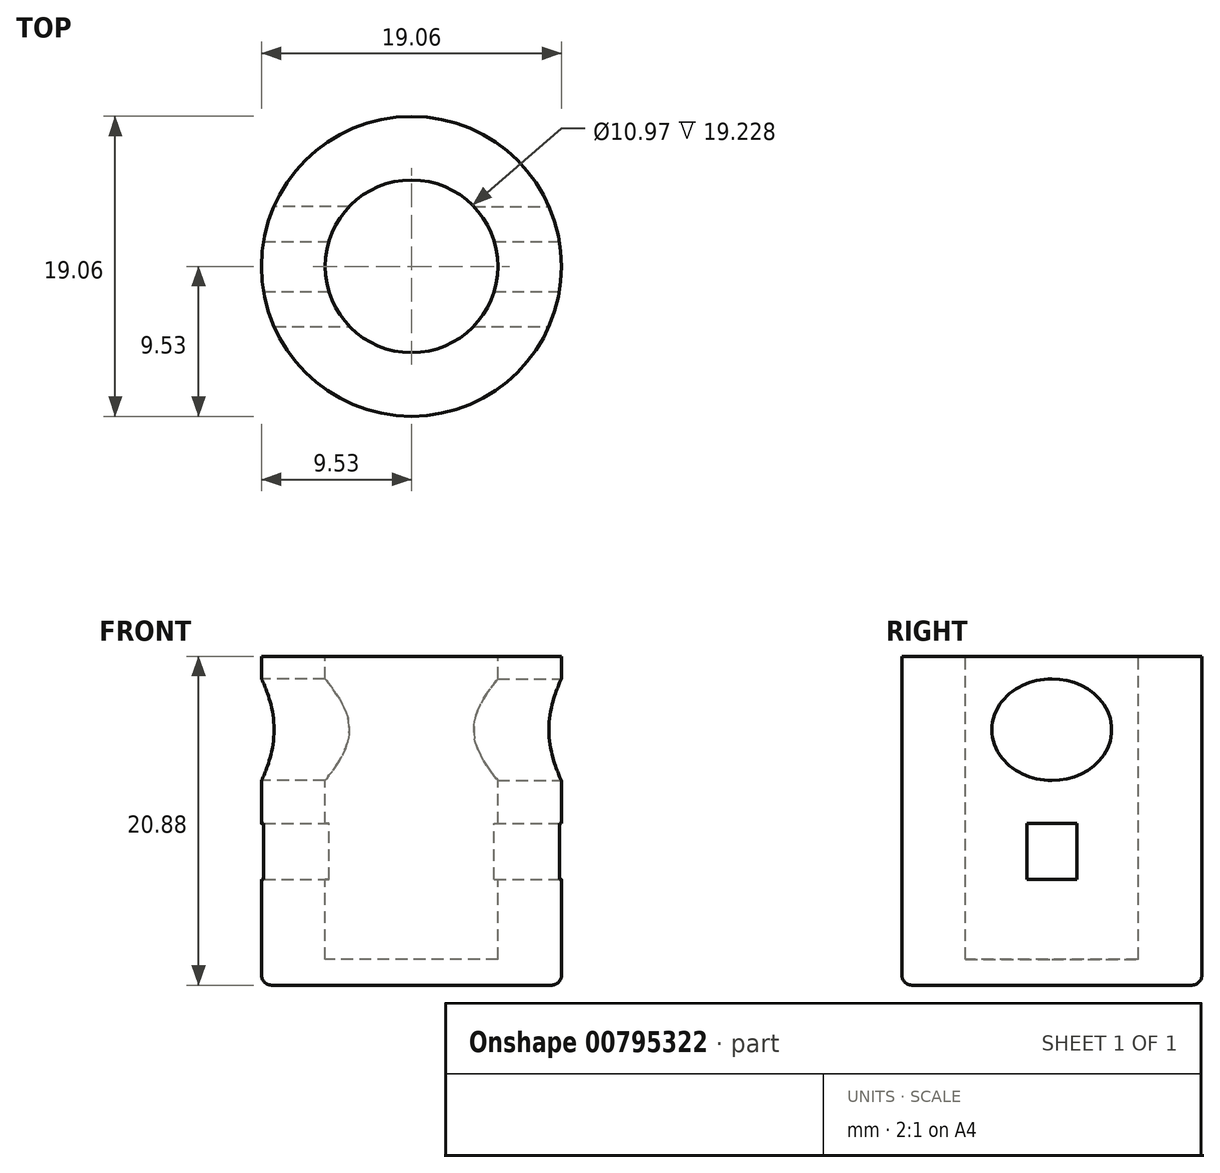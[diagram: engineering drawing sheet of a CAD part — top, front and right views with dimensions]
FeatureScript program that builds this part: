
annotation { "Feature Type Name" : "Feature", "Feature Type Description" : "" }
export const myFeature = defineFeature(function(context is Context, id is Id, definition is map)
    precondition{}
    {
        {
            var Q0;
            Q0=qCreatedBy(makeId("Top.planeOp"),FACE);
            var sketch = newSketch(context, id + "F0", { "sketchPlane" : qUnion([Q0])});
            skCircle(sketch, "E0", {"center": v(0, 0) * mm, "radius": 9.53 * mm});
            skSolve(sketch);
        }
        {
            var Q0;
            Q0=qSketchRegion(id+"F0",true);
            extrude(context, id + "F1", {"entities" : qUnion([Q0]), "endBound" : BoundingType.SYMMETRIC, "depth" : 20.88 * mm, "offsetDistance" : 25.4 * mm});
        }
        {
            var Q0;
            Q0=makeQuery(id+"F1.opExtrude","CAP_FACE",FACE,{"disambiguationData":[OSD([sQuery(id+"F0.wireOp",EDGE,"E0")])],"isStart":false});
            var sketch = newSketch(context, id + "F2", { "sketchPlane" : qUnion([Q0])});
            skCircle(sketch, "E1", {"center": v(0, 0) * mm, "radius": 5.49 * mm});
            skSolve(sketch);
        }
        {
            var Q0;
            Q0=qSketchRegion(id+"F2",true);
            extrude(context, id + "F3", {"entities" : qUnion([Q0]), "operationType" : NewBodyOperationType.REMOVE, "oppositeDirection" : true, "depth" : 19.23 * mm, "offsetDistance" : 25.4 * mm});
        }
        {
            var Q0;
            Q0=qCreatedBy(makeId("Right.planeOp"),FACE);
            var sketch = newSketch(context, id + "F4", { "sketchPlane" : qUnion([Q0])});
            skLineSegment(sketch, "E2.bottom", {"start": v(-1.59, -0.18) * mm, "end": v(1.59, -0.18) * mm});
            skLineSegment(sketch, "E2.top", {"start": v(-1.59, -3.7) * mm, "end": v(1.59, -3.7) * mm});
            skLineSegment(sketch, "E2.left", {"start": v(-1.59, -0.18) * mm, "end": v(-1.59, -3.7) * mm});
            skLineSegment(sketch, "E2.right", {"start": v(1.59, -0.18) * mm, "end": v(1.59, -3.7) * mm});
            skPoint(sketch, "E2.middle", {"position": v(0, -1.94) * mm});
            skSolve(sketch);
        }
        {
            var Q0;
            Q0=qSketchRegion(id+"F4",true);
            extrude(context, id + "F5", {"entities" : qUnion([Q0]), "operationType" : NewBodyOperationType.REMOVE, "endBound" : BoundingType.SYMMETRIC, "oppositeDirection" : true, "depth" : 25.4 * mm, "offsetDistance" : 25.4 * mm});
        }
        {
            var Q0;
            Q0=qCreatedBy(makeId("Right.planeOp"),FACE);
            var sketch = newSketch(context, id + "F6", { "sketchPlane" : qUnion([Q0])});
            skEllipse(sketch, "E3", {"center": v(0, 5.8) * mm, "majorRadius": 3.23 * mm, "minorRadius": 3.81 * mm, "majorAxis": v(0, 1)});
            skSolve(sketch);
        }
        {
            var Q0;
            Q0=qSketchRegion(id+"F6",true);
            extrude(context, id + "F7", {"entities" : qUnion([Q0]), "operationType" : NewBodyOperationType.REMOVE, "endBound" : BoundingType.SYMMETRIC, "oppositeDirection" : true, "depth" : 25.4 * mm, "offsetDistance" : 25.4 * mm});
        }
        {
            var Q0;
            Q0=makeQuery(id+"F1.opExtrude","CAP_EDGE",EDGE,{"disambiguationData":[OSD([sQuery(id+"F0.wireOp",EDGE,"E0")])],"isStart":true});
            fillet(context, id + "F8", {"entities" : qUnion([Q0]), "radius" : 0.64 * mm, "tangentPropagation" : true, "allowEdgeOverflow" : false});
        }
    });
